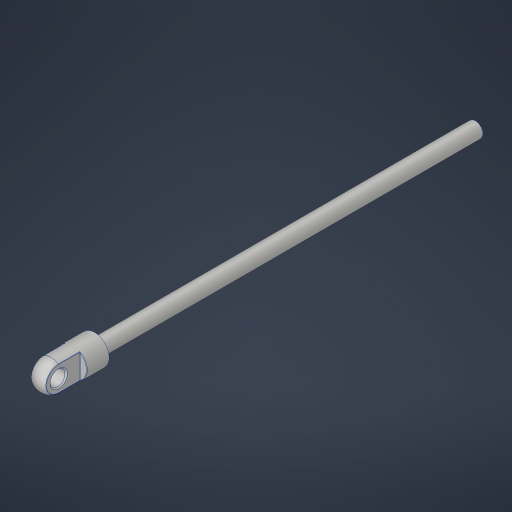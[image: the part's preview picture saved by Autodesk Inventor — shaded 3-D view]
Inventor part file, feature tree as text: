
AUTODESK INVENTOR PART (.ipt)
format: ipt  version: 2023.4 (Build 274418000, 418)  size: 328,192 bytes
history: native  units: in
note: dims shown in document units (in); Inventor stores cm internally (conversion verified against a paired STEP export)
features: fillet x2, other x2
ambient origin geometry x8: Origin, YZ Plane, XZ Plane, XY Plane, X Axis, Y Axis, Z Axis, Center Point
bodies: Solid1 (feature_tree), Solid2 (feature_tree), Solid3 (feature_tree), Solid4 (feature_tree)
feature tree (4):
  fillet  "Fillet5"  [1 undecoded]
  fillet  "Fillet6"  [1 undecoded]
  other  "Boss-Extrude1"
  other  "Cut-Extrude-Thin1"
note: 2 required parameter values undecoded (feature->parameter linkage not recoverable at this tier; creation-order binding heuristic only, values carry confidence <= 0.55)
